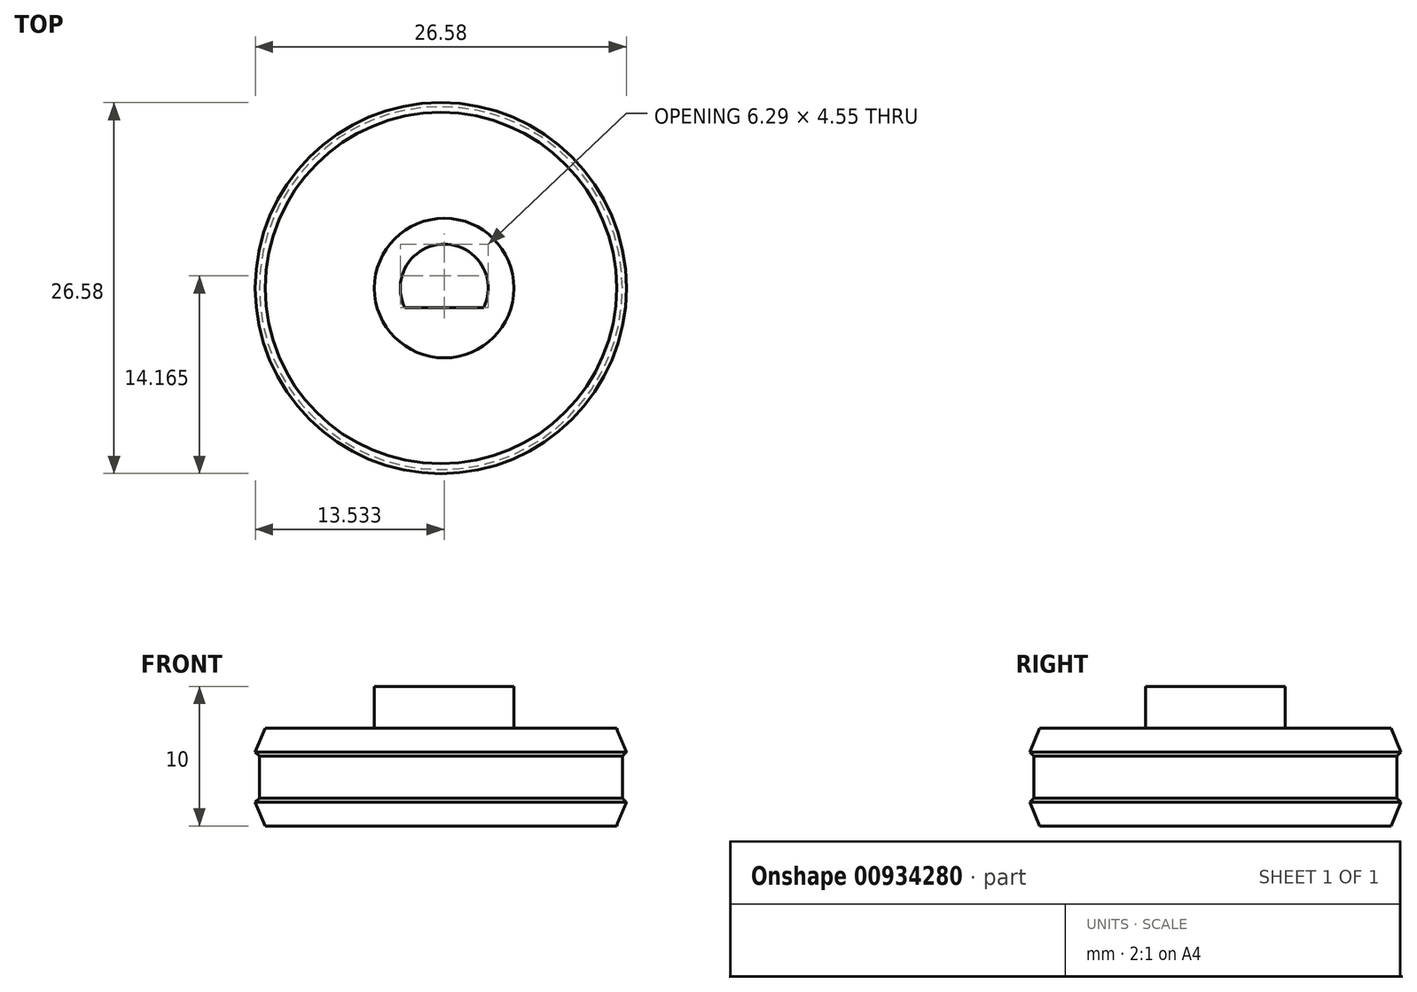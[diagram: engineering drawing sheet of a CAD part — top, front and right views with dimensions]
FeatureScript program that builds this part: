
annotation { "Feature Type Name" : "Feature", "Feature Type Description" : "" }
export const myFeature = defineFeature(function(context is Context, id is Id, definition is map)
    precondition{}
    {
        {
            var Q0;
            Q0=qCreatedBy(makeId("Top.planeOp"),FACE);
            var sketch = newSketch(context, id + "F0", { "sketchPlane" : qUnion([Q0])});
            skCircle(sketch, "E0", {"center": v(0, 0) * mm, "radius": 13 * mm});
            skSolve(sketch);
        }
        {
            var Q0;
            Q0=makeQuery(id+"F0.imprint","IMPRINT",FACE,{"disambiguationData":[TD([[makeQuery(id+"F0.imprint","IMPRINT",EDGE,{"derivedFrom":sQuery(id+"F0.wireOp",EDGE,"E0")}),1.0]])]});
            extrude(context, id + "F1", {"entities" : qUnion([Q0]), "depth" : 1.5 * mm, "offsetDistance" : 25 * mm});
        }
        {
            var Q0;
            Q0=makeQuery(id+"F1.opExtrude","CAP_FACE",FACE,{"disambiguationData":[OSD([sQuery(id+"F0.wireOp",EDGE,"E0")])],"isStart":false});
            var sketch = newSketch(context, id + "F2", { "sketchPlane" : qUnion([Q0])});
            skCircle(sketch, "E1", {"center": v(0, 0) * mm, "radius": 13 * mm});
            skSolve(sketch);
        }
        {
            var Q0;
            Q0=makeQuery(id+"F2.imprint","IMPRINT",FACE,{"disambiguationData":[TD([[makeQuery(id+"F2.imprint","IMPRINT",EDGE,{"derivedFrom":sQuery(id+"F2.wireOp",EDGE,"E1")}),1.0]])]});
            extrude(context, id + "F3", {"entities" : qUnion([Q0]), "operationType" : NewBodyOperationType.ADD, "depth" : 1.5 * mm, "offsetDistance" : 25 * mm});
        }
        {
            var Q0;
            Q0=makeQuery(id+"F3.opExtrude","CAP_FACE",FACE,{"disambiguationData":[OSD([sQuery(id+"F2.wireOp",EDGE,"E1")])],"isStart":false});
            var sketch = newSketch(context, id + "F4", { "sketchPlane" : qUnion([Q0])});
            skCircle(sketch, "E2", {"center": v(0.24, 0) * mm, "radius": 3.15 * mm});
            skCircle(sketch, "E3", {"center": v(0.24, 0) * mm, "radius": 5 * mm});
            skLineSegment(sketch, "E4", {"start": v(0.24, 3.15) * mm, "end": v(0.24, -1.4) * mm});
            skLineSegment(sketch, "E5", {"start": v(0.24, -1.4) * mm, "end": v(-3.37, -1.4) * mm});
            skLineSegment(sketch, "E6", {"start": v(0.24, -1.4) * mm, "end": v(4.1, -1.4) * mm});
            skSolve(sketch);
        }
        {
            var Q0;
            Q0=makeQuery(id+"F4.imprint","IMPRINT",FACE,{"disambiguationData":[TD([[makeQuery(id+"F4.imprint","IMPRINT",EDGE,{"derivedFrom":sQuery(id+"F4.wireOp",EDGE,"NRYqBuvR-jk6a-mnoZ-W9sO-KFZDdMpJj8ss")}),1.0]])]});
            var Q1;
            {var subQ0=sQuery(id+"F4.wireOp",EDGE,"PsRHYSWG-PZm0-3N33-hY3T-74irQeZ1qw2C");var subQ1=sQuery(id+"F4.wireOp",EDGE,"l4ecbsMB-e4FV-qC8y-9OMJ-fTEK3NTJFzOY");var subQ2=makeQuery(id+"F4.imprint","INTERSECT",VERTEX,{"derivedFrom":[subQ1,subQ0]});Q1=makeQuery(id+"F4.imprint","IMPRINT",FACE,{"disambiguationData":[TD([[makeQuery(id+"F4.imprint","IMPRINT",EDGE,{"disambiguationData":[TD([[subQ2,-1.0]])],"derivedFrom":subQ1}),1.0]])]});}
            var Q2;
            Q2=makeQuery(id+"F4.imprint","IMPRINT",FACE,{"disambiguationData":[TD([[makeQuery(id+"F4.imprint","IMPRINT",EDGE,{"derivedFrom":sQuery(id+"F4.wireOp",EDGE,"E3")}),1.0]])]});
            var Q3;
            {var subQ0=sQuery(id+"F4.wireOp",EDGE,"E5");var subQ1=sQuery(id+"F4.wireOp",EDGE,"E2");var subQ2=makeQuery(id+"F4.imprint","INTERSECT",VERTEX,{"derivedFrom":[subQ1,subQ0]});Q3=makeQuery(id+"F4.imprint","IMPRINT",FACE,{"disambiguationData":[TD([[makeQuery(id+"F4.imprint","IMPRINT",EDGE,{"disambiguationData":[TD([[subQ2,-1.0]])],"derivedFrom":subQ1}),1.0]])]});}
            extrude(context, id + "F5", {"entities" : qUnion([Q0, Q1, Q2, Q3]), "operationType" : NewBodyOperationType.ADD, "depth" : 5 * mm, "offsetDistance" : 25 * mm});
        }
        {
            var Q0;
            {var subQ0=sQuery(id+"F2.wireOp",EDGE,"E1");Q0=makeQuery(id+"F5.boolean.opBoolean","SPLIT",FACE,{"disambiguationData":[TD([makeQuery(id+"F1.opExtrude","SWEPT_FACE",FACE,{"disambiguationData":[OSD([sQuery(id+"F0.wireOp",EDGE,"E0")])]})])],"derivedFrom":makeQuery(id+"F3.opExtrude","CAP_FACE",FACE,{"disambiguationData":[OSD([subQ0])],"isStart":false})});}
            var sketch = newSketch(context, id + "F6", { "sketchPlane" : qUnion([Q0])});
            skCircle(sketch, "E7", {"center": v(0, 0) * mm, "radius": 15 * mm});
            skSolve(sketch);
        }
        {
            var Q0;
            Q0=makeQuery(id+"F1.opExtrude","CAP_FACE",FACE,{"disambiguationData":[OSD([sQuery(id+"F0.wireOp",EDGE,"E0")])],"isStart":true});
            var sketch = newSketch(context, id + "F7", { "sketchPlane" : qUnion([Q0])});
            skCircle(sketch, "E8", {"center": v(0, 0) * mm, "radius": 15 * mm});
            skSolve(sketch);
        }
        {
            var Q0;
            Q0=makeQuery(id+"F7.imprint","IMPRINT",FACE,{"disambiguationData":[TD([[makeQuery(id+"F7.imprint","IMPRINT",EDGE,{"derivedFrom":makeQuery(id+"F1.opExtrude","CAP_EDGE",EDGE,{"disambiguationData":[OSD([sQuery(id+"F0.wireOp",EDGE,"E0")])],"isStart":true})}),-1.0]])]});
            var Q1;
            Q1=makeQuery(id+"F7.imprint","IMPRINT",FACE,{"disambiguationData":[TD([[makeQuery(id+"F7.imprint","IMPRINT",EDGE,{"derivedFrom":sQuery(id+"F7.wireOp",EDGE,"E8")}),1.0]])]});
            extrude(context, id + "F8", {"entities" : qUnion([Q0, Q1]), "operationType" : NewBodyOperationType.ADD, "depth" : 2 * mm, "offsetDistance" : 25 * mm});
        }
        {
            var Q0;
            Q0=makeQuery(id+"F6.imprint","IMPRINT",FACE,{"disambiguationData":[TD([[makeQuery(id+"F6.imprint","IMPRINT",EDGE,{"derivedFrom":makeQuery(id+"F3.opExtrude","CAP_EDGE",EDGE,{"disambiguationData":[OSD([sQuery(id+"F2.wireOp",EDGE,"E1")])],"isStart":false})}),1.0]])]});
            var Q1;
            Q1=makeQuery(id+"F6.imprint","IMPRINT",FACE,{"disambiguationData":[TD([[makeQuery(id+"F6.imprint","IMPRINT",EDGE,{"derivedFrom":sQuery(id+"F6.wireOp",EDGE,"E7")}),1.0]])]});
            extrude(context, id + "F9", {"entities" : qUnion([Q0, Q1]), "operationType" : NewBodyOperationType.ADD, "depth" : 2 * mm, "offsetDistance" : 25 * mm});
        }
        {
            var Q0;
            Q0=makeQuery(id+"F9.opExtrude","CAP_EDGE",EDGE,{"disambiguationData":[OSD([sQuery(id+"F6.wireOp",EDGE,"E7")])],"isStart":true});
            var Q1;
            Q1=makeQuery(id+"F8.opExtrude","CAP_EDGE",EDGE,{"disambiguationData":[OSD([sQuery(id+"F7.wireOp",EDGE,"E8")])],"isStart":true});
            chamfer(context, id + "F10", {"entities" : qUnion([Q0, Q1]), "chamferType" : ChamferType.TWO_OFFSETS, "width1" : 2 * mm, "oppositeDirection" : false, "width2" : 2 * mm, "tangentPropagation" : true});
        }
        {
            var Q0;
            {var subQ0=sQuery(id+"F6.wireOp",EDGE,"E7");Q0=makeQuery(id+"F10.opChamfer","BLEND_EDGE",EDGE,{"blendedFrom":[makeQuery(id+"F9.opExtrude","CAP_EDGE",EDGE,{"disambiguationData":[OSD([subQ0])],"isStart":true}),makeQuery(id+"F9.opExtrude","CAP_FACE",FACE,{"disambiguationData":[OSD([sQuery(id+"F4.wireOp",EDGE,"NRYqBuvR-jk6a-mnoZ-W9sO-KFZDdMpJj8ss"),subQ0])],"isStart":false})],"blendedInto":[makeQuery(id+"F9.opExtrude","CAP_FACE",FACE,{"disambiguationData":[OSD([sQuery(id+"F4.wireOp",EDGE,"NRYqBuvR-jk6a-mnoZ-W9sO-KFZDdMpJj8ss"),subQ0])],"isStart":false})]});}
            var Q1;
            {var subQ0=sQuery(id+"F7.wireOp",EDGE,"E8");Q1=makeQuery(id+"F10.opChamfer","BLEND_EDGE",EDGE,{"blendedFrom":[makeQuery(id+"F8.opExtrude","CAP_EDGE",EDGE,{"disambiguationData":[OSD([subQ0])],"isStart":true}),makeQuery(id+"F8.opExtrude","CAP_FACE",FACE,{"disambiguationData":[OSD([subQ0])],"isStart":false})],"blendedInto":[makeQuery(id+"F8.opExtrude","CAP_FACE",FACE,{"disambiguationData":[OSD([subQ0])],"isStart":false})]});}
            chamfer(context, id + "F11", {"entities" : qUnion([Q0, Q1]), "width" : 1 * mm, "tangentPropagation" : true});
        }
        {
            var Q0;
            {var subQ0=sQuery(id+"F4.wireOp",EDGE,"E4");Q0=makeQuery(id+"F4.imprint","IMPRINT",FACE,{"disambiguationData":[TD([[makeQuery(id+"F4.imprint","IMPRINT",EDGE,{"derivedFrom":subQ0}),-1.0]])]});}
            var Q1;
            {var subQ0=sQuery(id+"F4.wireOp",EDGE,"E4");Q1=makeQuery(id+"F4.imprint","IMPRINT",FACE,{"disambiguationData":[TD([[makeQuery(id+"F4.imprint","IMPRINT",EDGE,{"derivedFrom":subQ0}),1.0]])]});}
            extrude(context, id + "F12", {"entities" : qUnion([Q0, Q1]), "operationType" : NewBodyOperationType.REMOVE, "oppositeDirection" : true, "depth" : 25 * mm, "offsetDistance" : 25 * mm});
        }
    });
